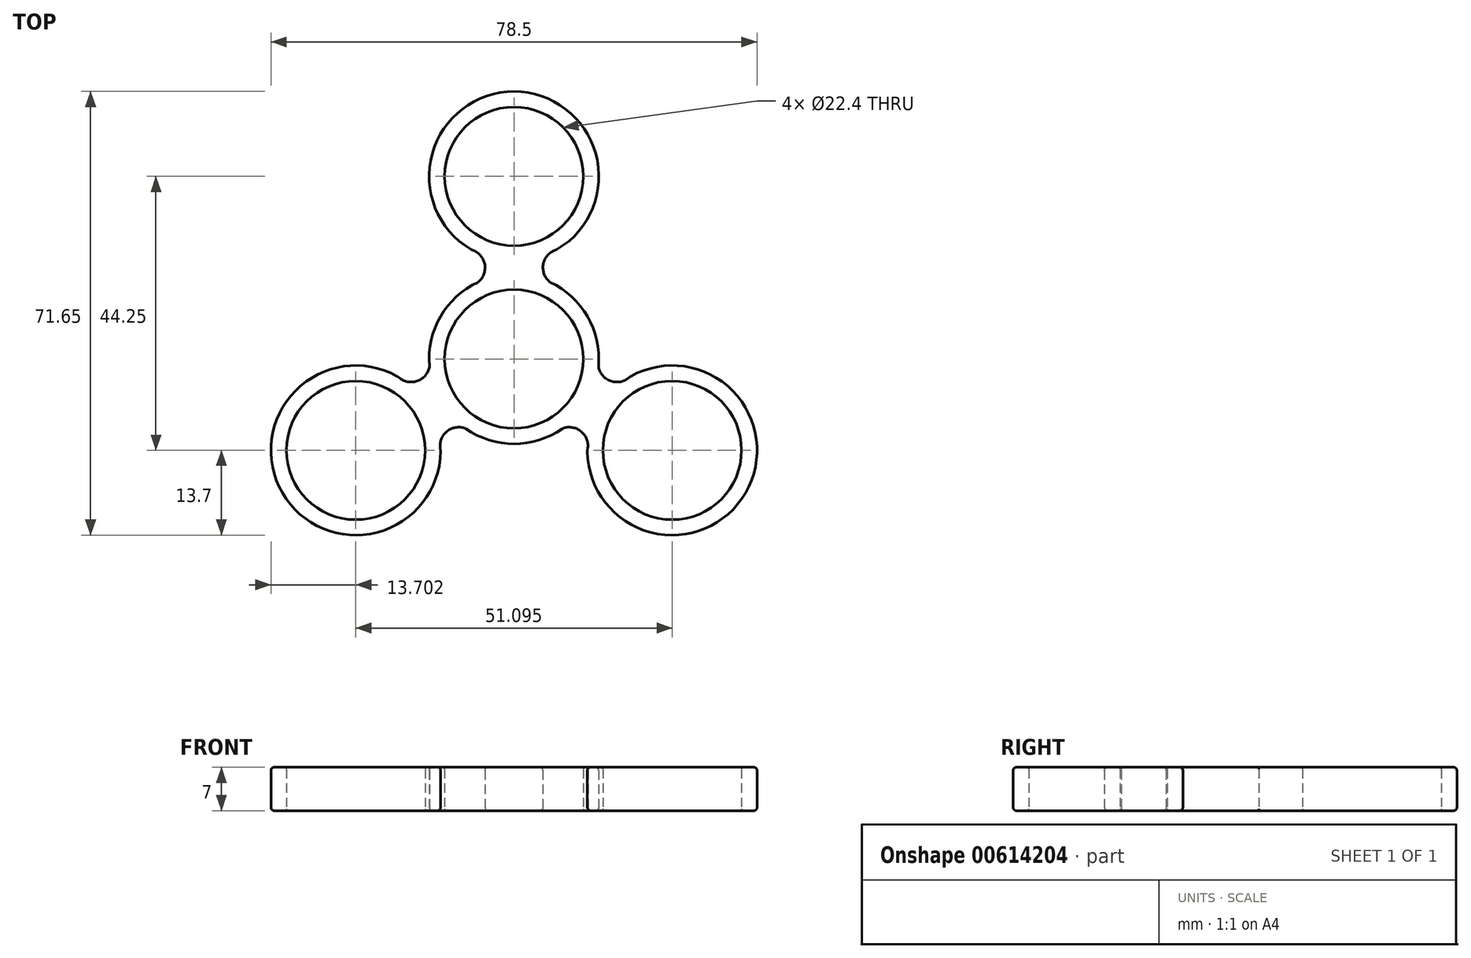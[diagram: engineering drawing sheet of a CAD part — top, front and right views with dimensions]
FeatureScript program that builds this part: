
annotation { "Feature Type Name" : "Feature", "Feature Type Description" : "" }
export const myFeature = defineFeature(function(context is Context, id is Id, definition is map)
    precondition{}
    {
        {
            var Q0;
            Q0=qCreatedBy(makeId("Top.planeOp"),FACE);
            var sketch = newSketch(context, id + "F0", { "sketchPlane" : qUnion([Q0])});
            skCircle(sketch, "E0", {"center": v(0, 0) * mm, "radius": 11.2 * mm});
            skArc(sketch, "E1.0", {"start": v(-5.2, 12.68) * mm, "mid": v(-5.5, 12.55) * mm, "end": v(-5.79, 12.42) * mm, "construction": true});
            skLineSegment(sketch, "E2", {"start": v(0, 0) * mm, "end": v(0, 29.5) * mm, "construction": true});
            skCircle(sketch, "E3", {"center": v(0, 29.5) * mm, "radius": 11.2 * mm});
            skArc(sketch, "E4.0", {"start": v(7, 17.72) * mm, "mid": v(0, 43.2) * mm, "end": v(-7, 17.72) * mm});
            skPoint(sketch, "E5.visualSharp", {"position": v(0, 14.75) * mm});
            skLineSegment(sketch, "E6.0", {"start": v(7, 0) * mm, "end": v(7, 29.5) * mm, "construction": true});
            skLineSegment(sketch, "E7", {"start": v(7, 17.72) * mm, "end": v(6.5, 17.51) * mm});
            skLineSegment(sketch, "E8", {"start": v(6.5, 11.99) * mm, "end": v(7, 11.78) * mm});
            skArc(sketch, "E9.filletArc", {"start": v(6.5, 17.51) * mm, "mid": v(4.67, 14.75) * mm, "end": v(6.5, 11.99) * mm});
            skLineSegment(sketch, "E10.MirrorCS", {"start": v(-7, 17.72) * mm, "end": v(-6.5, 17.51) * mm});
            skLineSegment(sketch, "E11.MirrorCS", {"start": v(-6.5, 11.99) * mm, "end": v(-7, 11.78) * mm});
            skArc(sketch, "E12.MirrorCS", {"start": v(-6.5, 17.51) * mm, "mid": v(-4.67, 14.75) * mm, "end": v(-6.5, 11.99) * mm});
            skArc(sketch, "E13.trimOffspring", {"start": v(-7, 11.78) * mm, "mid": v(0, -13.7) * mm, "end": v(7, 11.78) * mm});
            skSolve(sketch);
        }
        {
            var Q0;
            Q0 = qSketchRegion(id + "F2", true);
            var Q1;
            Q1 = qSketchRegion(id + "F0", true);
            extrude(context, id + "F1", {"entities" : qUnion([Q0, Q1]), "depth" : 7 * mm, "offsetDistance" : 25 * mm});
        }
        {
            var Q0;
            Q0=qCreatedBy(makeId("Right.planeOp"),FACE);
            var sketch = newSketch(context, id + "F2", { "sketchPlane" : qUnion([Q0])});
            skLineSegment(sketch, "E14", {"start": v(0, -11.35) * mm, "end": v(0, 14.45) * mm, "construction": true});
            skSolve(sketch);
        }
        {
            var Q0;
            Q0=makeQuery(id+"F1.opExtrude","SWEPT_BODY",BODY,{"disambiguationData":[OSD([sQuery(id+"F0.wireOp",EDGE,"E0"),sQuery(id+"F0.wireOp",EDGE,"E1.0"),sQuery(id+"F0.wireOp",EDGE,"E3"),sQuery(id+"F0.wireOp",EDGE,"E4.0"),sQuery(id+"F0.wireOp",EDGE,"7c884c8c-e37f-41f7-9a8e-9150e4511ce8.0"),sQuery(id+"F0.wireOp",EDGE,"124d70be-8a2f-4ff1-8067-023c3a760d13.0"),sQuery(id+"F0.wireOp",EDGE,"7qioyo7K-iHsX-Xa6s-X97m-BwtuQXfGrCvp"),sQuery(id+"F0.wireOp",EDGE,"oFAU7C9Q-nsB6-dseo-MMuZ-7hNLlDQCrwbt"),sQuery(id+"F0.wireOp",EDGE,"a2486781-22df-47b1-8026-fe576fbc433f.0"),sQuery(id+"F0.wireOp",EDGE,"cb9c9ce2-17e4-408e-8bf5-b38f411324f0.0"),sQuery(id+"F0.wireOp",EDGE,"jKmUo85i-UXFQ-YKQP-mafa-QPdGbBQ2pSZu"),sQuery(id+"F0.wireOp",EDGE,"14rnQz0T-OoW9-SuH9-BmvN-4Fd0IeYT7QfG")])]});
            var Q1;
            Q1=sQuery(id+"F2.wireOp",EDGE,"E14");
            circularPattern(context, id + "F3", {"operationType" : NewBodyOperationType.ADD, "entities" : qUnion([Q0]), "axis" : qUnion([Q1]), "angle" : 360 * degree, "instanceCount" : 3, "equalSpace" : true});
        }
        {
            var Q0;
            {var subQ0=makeQuery(id+"F1.opExtrude","SWEPT_FACE",FACE,{"disambiguationData":[OSD([sQuery(id+"F0.wireOp",EDGE,"E13.trimOffspring")])]});Q0=makeQuery(id+"F3.boolean.opBoolean","MERGE",FACE,{"disambiguationData":[OD(1.0)],"derivedFrom":[subQ0,makeQuery(id+"F3.opPattern","COPY",FACE,{"derivedFrom":subQ0,"instanceName":"1"}),makeQuery(id+"F3.opPattern","COPY",FACE,{"derivedFrom":subQ0,"instanceName":"2"})]});}
            var Q1;
            Q1=makeQuery(id+"F3.opPattern","COPY",FACE,{"derivedFrom":makeQuery(id+"F1.opExtrude","SWEPT_FACE",FACE,{"disambiguationData":[OSD([sQuery(id+"F0.wireOp",EDGE,"E4.0")])]}),"instanceName":"1"});
            var Q2;
            Q2=makeQuery(id+"F3.boolean.opBoolean","SPLIT",FACE,{"derivedFrom":makeQuery(id+"F1.opExtrude","SWEPT_FACE",FACE,{"disambiguationData":[OSD([sQuery(id+"F0.wireOp",EDGE,"E13.trimOffspring")])]})});
            var Q3;
            Q3=makeQuery(id+"F3.opPattern","COPY",FACE,{"derivedFrom":makeQuery(id+"F1.opExtrude","SWEPT_FACE",FACE,{"disambiguationData":[OSD([sQuery(id+"F0.wireOp",EDGE,"E12.MirrorCS")])]}),"instanceName":"1"});
            var Q4;
            Q4=makeQuery(id+"F3.opPattern","COPY",FACE,{"derivedFrom":makeQuery(id+"F1.opExtrude","SWEPT_FACE",FACE,{"disambiguationData":[OSD([sQuery(id+"F0.wireOp",EDGE,"E9.filletArc")])]}),"instanceName":"1"});
            var Q5;
            Q5=makeQuery(id+"F3.opPattern","COPY",FACE,{"derivedFrom":makeQuery(id+"F1.opExtrude","SWEPT_FACE",FACE,{"disambiguationData":[OSD([sQuery(id+"F0.wireOp",EDGE,"E9.filletArc")])]}),"instanceName":"2"});
            var Q6;
            Q6=makeQuery(id+"F3.opPattern","COPY",FACE,{"derivedFrom":makeQuery(id+"F1.opExtrude","SWEPT_FACE",FACE,{"disambiguationData":[OSD([sQuery(id+"F0.wireOp",EDGE,"E4.0")])]}),"instanceName":"2"});
            var Q7;
            Q7=makeQuery(id+"F3.opPattern","COPY",FACE,{"derivedFrom":makeQuery(id+"F1.opExtrude","SWEPT_FACE",FACE,{"disambiguationData":[OSD([sQuery(id+"F0.wireOp",EDGE,"E12.MirrorCS")])]}),"instanceName":"2"});
            var Q8;
            {var subQ0=makeQuery(id+"F1.opExtrude","SWEPT_FACE",FACE,{"disambiguationData":[OSD([sQuery(id+"F0.wireOp",EDGE,"E13.trimOffspring")])]});Q8=makeQuery(id+"F3.boolean.opBoolean","MERGE",FACE,{"disambiguationData":[OD(0.0)],"derivedFrom":[subQ0,makeQuery(id+"F3.opPattern","COPY",FACE,{"derivedFrom":subQ0,"instanceName":"1"}),makeQuery(id+"F3.opPattern","COPY",FACE,{"derivedFrom":subQ0,"instanceName":"2"})]});}
            var Q9;
            Q9=makeQuery(id+"F1.opExtrude","SWEPT_FACE",FACE,{"disambiguationData":[OSD([sQuery(id+"F0.wireOp",EDGE,"E9.filletArc")])]});
            var Q10;
            Q10=makeQuery(id+"F1.opExtrude","SWEPT_FACE",FACE,{"disambiguationData":[OSD([sQuery(id+"F0.wireOp",EDGE,"E4.0")])]});
            var Q11;
            Q11=makeQuery(id+"F1.opExtrude","SWEPT_FACE",FACE,{"disambiguationData":[OSD([sQuery(id+"F0.wireOp",EDGE,"E12.MirrorCS")])]});
            fillet(context, id + "F4", {"entities" : qUnion([Q0, Q1, Q2, Q3, Q4, Q5, Q6, Q7, Q8, Q9, Q10, Q11]), "radius" : 0.5 * mm, "tangentPropagation" : true, "allowEdgeOverflow" : false});
        }
        {
            var Q0;
            Q0=makeQuery(id+"F1.opExtrude","SWEPT_FACE",FACE,{"disambiguationData":[OSD([sQuery(id+"F0.wireOp",EDGE,"E3")])]});
            var Q1;
            Q1=makeQuery(id+"F1.opExtrude","SWEPT_FACE",FACE,{"disambiguationData":[OSD([sQuery(id+"F0.wireOp",EDGE,"E0")])]});
            var Q2;
            Q2=makeQuery(id+"F3.opPattern","COPY",FACE,{"derivedFrom":makeQuery(id+"F1.opExtrude","SWEPT_FACE",FACE,{"disambiguationData":[OSD([sQuery(id+"F0.wireOp",EDGE,"E3")])]}),"instanceName":"2"});
            var Q3;
            Q3=makeQuery(id+"F3.opPattern","COPY",FACE,{"derivedFrom":makeQuery(id+"F1.opExtrude","SWEPT_FACE",FACE,{"disambiguationData":[OSD([sQuery(id+"F0.wireOp",EDGE,"E3")])]}),"instanceName":"1"});
            fillet(context, id + "F5", {"entities" : qUnion([Q0, Q1, Q2, Q3]), "radius" : 0.3 * mm, "tangentPropagation" : true, "allowEdgeOverflow" : false});
        }
    });
